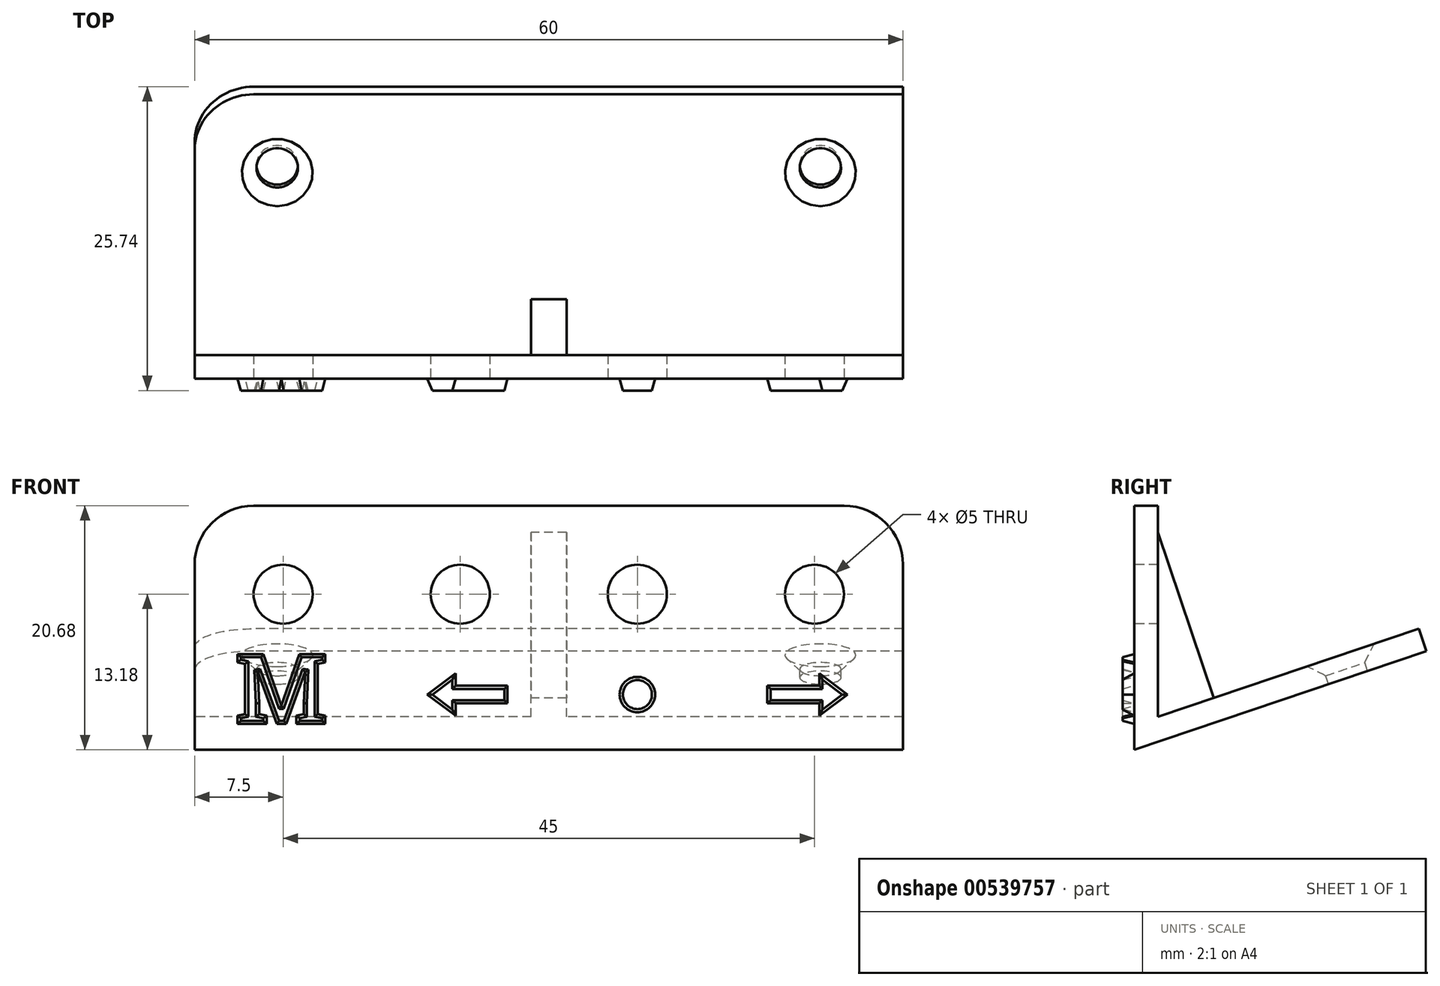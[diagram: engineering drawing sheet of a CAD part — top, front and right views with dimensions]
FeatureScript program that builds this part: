
annotation { "Feature Type Name" : "Feature", "Feature Type Description" : "" }
export const myFeature = defineFeature(function(context is Context, id is Id, definition is map)
    precondition{}
    {
        {
            var Q0;
            Q0=qCreatedBy(makeId("Front.planeOp"),FACE);
            var sketch = newSketch(context, id + "F0", { "sketchPlane" : qUnion([Q0])});
            skCircle(sketch, "E0", {"center": v(0, 0) * mm, "radius": 2.5 * mm});
            skCircle(sketch, "E1.1.0.0", {"center": v(15, 0) * mm, "radius": 2.5 * mm});
            skCircle(sketch, "E1.2.0.0", {"center": v(30, 0) * mm, "radius": 2.5 * mm});
            skCircle(sketch, "E1.3.0.0", {"center": v(45, 0) * mm, "radius": 2.5 * mm});
            skLineSegment(sketch, "E1.direction1", {"start": v(0, 0) * mm, "end": v(15, 0) * mm, "construction": true});
            skLineSegment(sketch, "E2.bottom", {"start": v(-7.5, -12.5) * mm, "end": v(52.5, -12.5) * mm});
            skLineSegment(sketch, "E2.top", {"start": v(-7.5, 7.5) * mm, "end": v(52.5, 7.5) * mm});
            skLineSegment(sketch, "E2.left", {"start": v(-7.5, -12.5) * mm, "end": v(-7.5, 7.5) * mm});
            skLineSegment(sketch, "E2.right", {"start": v(52.5, -12.5) * mm, "end": v(52.5, 7.5) * mm});
            skText(sketch, "E3", { "text": "M", "fontName": "RobotoSlab-Bold.ttf"});
            skLineSegment(sketch, "E4", {"start": v(41, -7.75) * mm, "end": v(45.4, -7.75) * mm});
            skLineSegment(sketch, "E5", {"start": v(45.4, -7.75) * mm, "end": v(45.4, -6.7) * mm});
            skLineSegment(sketch, "E6", {"start": v(45.4, -6.7) * mm, "end": v(47.8, -8.5) * mm});
            skLineSegment(sketch, "E7", {"start": v(47.8, -8.5) * mm, "end": v(45.4, -10.3) * mm});
            skLineSegment(sketch, "E8", {"start": v(45.4, -10.3) * mm, "end": v(45.4, -9.25) * mm});
            skLineSegment(sketch, "E9", {"start": v(45.4, -9.25) * mm, "end": v(41, -9.25) * mm});
            skLineSegment(sketch, "E10", {"start": v(41, -9.25) * mm, "end": v(41, -7.75) * mm});
            skLineSegment(sketch, "E11", {"start": v(41, -8.5) * mm, "end": v(47.8, -8.5) * mm, "construction": true});
            skLineSegment(sketch, "E12", {"start": v(30, 0) * mm, "end": v(30, -12.5) * mm, "construction": true});
            skLineSegment(sketch, "E13.MirrorCS", {"start": v(14.6, -10.3) * mm, "end": v(14.6, -9.25) * mm});
            skLineSegment(sketch, "E14.MirrorCS", {"start": v(19, -7.75) * mm, "end": v(14.6, -7.75) * mm});
            skLineSegment(sketch, "E15.MirrorCS", {"start": v(19, -8.5) * mm, "end": v(12.2, -8.5) * mm, "construction": true});
            skLineSegment(sketch, "E16.MirrorCS", {"start": v(14.6, -9.25) * mm, "end": v(19, -9.25) * mm});
            skLineSegment(sketch, "E17.MirrorCS", {"start": v(12.2, -8.5) * mm, "end": v(14.6, -10.3) * mm});
            skLineSegment(sketch, "E18.MirrorCS", {"start": v(14.6, -6.7) * mm, "end": v(12.2, -8.5) * mm});
            skLineSegment(sketch, "E19.MirrorCS", {"start": v(19, -9.25) * mm, "end": v(19, -7.75) * mm});
            skLineSegment(sketch, "E20.MirrorCS", {"start": v(14.6, -7.75) * mm, "end": v(14.6, -6.7) * mm});
            skCircle(sketch, "E21", {"center": v(30, -8.5) * mm, "radius": 1.5 * mm});
            skLineSegment(sketch, "E22.bottom", {"start": v(-9.5, -14.5) * mm, "end": v(54.5, -14.5) * mm});
            skLineSegment(sketch, "E22.top", {"start": v(-9.5, 9.5) * mm, "end": v(54.5, 9.5) * mm});
            skLineSegment(sketch, "E22.left", {"start": v(-9.5, -14.5) * mm, "end": v(-9.5, 9.5) * mm});
            skLineSegment(sketch, "E22.right", {"start": v(54.5, -14.5) * mm, "end": v(54.5, 9.5) * mm});
            const initialGuessF0  = {"E3": [-0.00408, -0.011, 1, 0, 0.006]};
            skSetInitialGuess(sketch, initialGuessF0);
            skSolve(sketch);
        }
        {
            var Q0;
            Q0=makeQuery(id+"F0.imprint","IMPRINT",FACE,{"disambiguationData":[TD([[makeQuery(id+"F0.imprint","IMPRINT",EDGE,{"derivedFrom":sQuery(id+"F0.wireOp",EDGE,"E0")}),-1.0]])]});
            var Q1;
            Q1=makeQuery(id+"F0.imprint","IMPRINT",FACE,{"disambiguationData":[TD([[makeQuery(id+"F0.imprint","IMPRINT",EDGE,{"derivedFrom":sQuery(id+"F0.wireOp",EDGE,"E3.sketch_text.stroke-0")}),-1.0]])]});
            var Q2;
            Q2=makeQuery(id+"F0.imprint","IMPRINT",FACE,{"disambiguationData":[TD([[makeQuery(id+"F0.imprint","IMPRINT",EDGE,{"derivedFrom":sQuery(id+"F0.wireOp",EDGE,"E13.MirrorCS")}),1.0]])]});
            var Q3;
            Q3=makeQuery(id+"F0.imprint","IMPRINT",FACE,{"disambiguationData":[TD([[makeQuery(id+"F0.imprint","IMPRINT",EDGE,{"derivedFrom":sQuery(id+"F0.wireOp",EDGE,"E21")}),1.0]])]});
            var Q4;
            Q4=makeQuery(id+"F0.imprint","IMPRINT",FACE,{"disambiguationData":[TD([[makeQuery(id+"F0.imprint","IMPRINT",EDGE,{"derivedFrom":sQuery(id+"F0.wireOp",EDGE,"E4")}),-1.0]])]});
            extrude(context, id + "F1", {"entities" : qUnion([Q0, Q1, Q2, Q3, Q4]), "oppositeDirection" : true, "depth" : 2 * mm, "offsetDistance" : 25 * mm});
        }
        {
            var Q0;
            Q0=makeQuery(id+"F0.imprint","IMPRINT",FACE,{"disambiguationData":[TD([[makeQuery(id+"F0.imprint","IMPRINT",EDGE,{"derivedFrom":sQuery(id+"F0.wireOp",EDGE,"E3.sketch_text.stroke-0")}),-1.0]])]});
            var Q1;
            Q1=makeQuery(id+"F0.imprint","IMPRINT",FACE,{"disambiguationData":[TD([[makeQuery(id+"F0.imprint","IMPRINT",EDGE,{"derivedFrom":sQuery(id+"F0.wireOp",EDGE,"E13.MirrorCS")}),1.0]])]});
            var Q2;
            Q2=makeQuery(id+"F0.imprint","IMPRINT",FACE,{"disambiguationData":[TD([[makeQuery(id+"F0.imprint","IMPRINT",EDGE,{"derivedFrom":sQuery(id+"F0.wireOp",EDGE,"E21")}),1.0]])]});
            var Q3;
            Q3=makeQuery(id+"F0.imprint","IMPRINT",FACE,{"disambiguationData":[TD([[makeQuery(id+"F0.imprint","IMPRINT",EDGE,{"derivedFrom":sQuery(id+"F0.wireOp",EDGE,"E4")}),-1.0]])]});
            extrude(context, id + "F2", {"entities" : qUnion([Q0, Q1, Q2, Q3]), "operationType" : NewBodyOperationType.ADD, "depth" : 1 * mm, "offsetDistance" : 25 * mm, "hasDraft" : true, "draftAngle" : 15 * degree, "draftPullDirection" : true});
        }
        {
            var Q0;
            Q0=makeQuery(id+"F1.opExtrude","SWEPT_FACE",FACE,{"disambiguationData":[OSD([sQuery(id+"F0.wireOp",EDGE,"E2.left")])]});
            var sketch = newSketch(context, id + "F3", { "sketchPlane" : qUnion([Q0])});
            skLineSegment(sketch, "E23", {"start": v(-2, -12.5) * mm, "end": v(-24.74, -4.82) * mm});
            skLineSegment(sketch, "E24", {"start": v(-24.74, -4.82) * mm, "end": v(-24.1, -2.92) * mm});
            skLineSegment(sketch, "E25", {"start": v(-24.1, -2.92) * mm, "end": v(-2, -10.39) * mm});
            skLineSegment(sketch, "E26", {"start": v(-2, -12.5) * mm, "end": v(0, -13.18) * mm});
            skLineSegment(sketch, "E27", {"start": v(0, -13.18) * mm, "end": v(0, -12.5) * mm});
            skSolve(sketch);
        }
        {
            var Q0;
            {var subQ0=sQuery(id+"F3.wireOp",EDGE,"E23");Q0=makeQuery(id+"F3.imprint","IMPRINT",FACE,{"disambiguationData":[TD([[makeQuery(id+"F3.imprint","IMPRINT",EDGE,{"derivedFrom":subQ0}),-1.0]])]});}
            var Q1;
            Q1=makeQuery(id+"F3.imprint","IMPRINT",FACE,{"disambiguationData":[TD([[makeQuery(id+"F3.imprint","IMPRINT",EDGE,{"derivedFrom":sQuery(id+"F3.wireOp",EDGE,"E26")}),1.0]])]});
            var Q2;
            Q2=makeQuery(id+"F1.opExtrude","SWEPT_FACE",FACE,{"disambiguationData":[OSD([sQuery(id+"F0.wireOp",EDGE,"E2.right")])]});
            extrude(context, id + "F4", {"entities" : qUnion([Q0, Q1]), "operationType" : NewBodyOperationType.ADD, "endBound" : BoundingType.UP_TO_SURFACE, "oppositeDirection" : true, "depth" : 25 * mm, "endBoundEntityFace" : qUnion([Q2]), "offsetDistance" : 25 * mm});
        }
        {
            var Q0;
            Q0=makeQuery(id+"F4.opExtrude","SWEPT_FACE",FACE,{"disambiguationData":[OSD([sQuery(id+"F3.wireOp",EDGE,"E25")])]});
            var sketch = newSketch(context, id + "F5", { "sketchPlane" : qUnion([Q0])});
            skPoint(sketch, "E28", {"position": v(45.5, 14.9) * mm});
            skLineSegment(sketch, "E29", {"start": v(22.5, 21.9) * mm, "end": v(22.5, -9.9) * mm, "construction": true});
            skPoint(sketch, "E30.MirrorP", {"position": v(-0.5, 14.9) * mm});
            skLineSegment(sketch, "E31.bottom", {"start": v(24, -1.43) * mm, "end": v(21, -1.43) * mm});
            skLineSegment(sketch, "E31.top", {"start": v(24, 3.57) * mm, "end": v(21, 3.57) * mm});
            skLineSegment(sketch, "E31.left", {"start": v(24, -1.43) * mm, "end": v(24, 3.57) * mm});
            skLineSegment(sketch, "E31.right", {"start": v(21, -1.43) * mm, "end": v(21, 3.57) * mm});
            skSolve(sketch);
        }
        {
            var Q0;
            Q0=sQuery(id+"F5.wireOp",VERTEX,"E28");
            var Q1;
            Q1=sQuery(id+"F5.wireOp",VERTEX,"E30.MirrorP");
            var Q2;
            Q2=makeQuery(id+"F1.opExtrude","SWEPT_BODY",BODY,{"disambiguationData":[OSD([sQuery(id+"F0.wireOp",EDGE,"E0"),sQuery(id+"F0.wireOp",EDGE,"E1.1.0.0"),sQuery(id+"F0.wireOp",EDGE,"E1.2.0.0"),sQuery(id+"F0.wireOp",EDGE,"E1.3.0.0"),sQuery(id+"F0.wireOp",EDGE,"E2.bottom"),sQuery(id+"F0.wireOp",EDGE,"E2.top"),sQuery(id+"F0.wireOp",EDGE,"E2.left"),sQuery(id+"F0.wireOp",EDGE,"E2.right")])]});
            hole(context, id + "F6", {"style" : HoleStyle.C_SINK, "endStyle" : HoleEndStyle.THROUGH, "holeDiameter" : 3.5 * mm, "cSinkDiameter" : 6 * mm, "cSinkAngle" : 90 * degree, "majorDiameter" : 5 * mm, "isTappedThrough" : true, "tappedDepth" : 12 * mm, "tapClearance" : 3, "locations" : qUnion([Q0, Q1]), "scope" : qUnion([Q2])});
        }
        {
            var Q0;
            Q0=makeQuery(id+"F1.opExtrude","SWEPT_EDGE",EDGE,{"disambiguationData":[OSD([sQuery(id+"F0.wireOp",EDGE,"E2.top"),sQuery(id+"F0.wireOp",EDGE,"E2.left")])]});
            var Q1;
            Q1=makeQuery(id+"F1.opExtrude","SWEPT_EDGE",EDGE,{"disambiguationData":[OSD([sQuery(id+"F0.wireOp",EDGE,"E2.top"),sQuery(id+"F0.wireOp",EDGE,"E2.right")])]});
            var Q2;
            Q2=makeQuery(id+"F4.opExtrude","CAP_EDGE",EDGE,{"disambiguationData":[OSD([sQuery(id+"F3.wireOp",EDGE,"E24")])],"isStart":true});
            var Q3;
            Q3=makeQuery(id+"F4.opExtrude","TWEAK_EDGE",EDGE,{"derivedFrom":[makeQuery(id+"F1.opExtrude","SWEPT_FACE",FACE,{"disambiguationData":[OSD([sQuery(id+"F0.wireOp",EDGE,"E2.right")])]}),makeQuery(id+"F3.imprint","IMPRINT",EDGE,{"derivedFrom":sQuery(id+"F3.wireOp",EDGE,"E24")})]});
            fillet(context, id + "F7", {"entities" : qUnion([Q0, Q1, Q2, Q3]), "radius" : 5 * mm, "tangentPropagation" : true, "allowEdgeOverflow" : false});
        }
        {
            var Q0;
            Q0=makeQuery(id+"F5.imprint","IMPRINT",FACE,{"disambiguationData":[TD([[makeQuery(id+"F5.imprint","IMPRINT",EDGE,{"derivedFrom":sQuery(id+"F5.wireOp",EDGE,"E31.bottom")}),-1.0]])]});
            var Q1;
            Q1=makeQuery(id+"F1.opExtrude","CAP_FACE",FACE,{"disambiguationData":[OSD([sQuery(id+"F0.wireOp",EDGE,"E0"),sQuery(id+"F0.wireOp",EDGE,"E1.1.0.0"),sQuery(id+"F0.wireOp",EDGE,"E1.2.0.0"),sQuery(id+"F0.wireOp",EDGE,"E1.3.0.0"),sQuery(id+"F0.wireOp",EDGE,"E2.bottom"),sQuery(id+"F0.wireOp",EDGE,"E2.top"),sQuery(id+"F0.wireOp",EDGE,"E2.left"),sQuery(id+"F0.wireOp",EDGE,"E2.right")])],"isStart":false});
            extrude(context, id + "F8", {"entities" : qUnion([Q0]), "operationType" : NewBodyOperationType.ADD, "endBound" : BoundingType.UP_TO_SURFACE, "depth" : 25 * mm, "endBoundEntityFace" : qUnion([Q1]), "offsetDistance" : 25 * mm});
        }
    });
